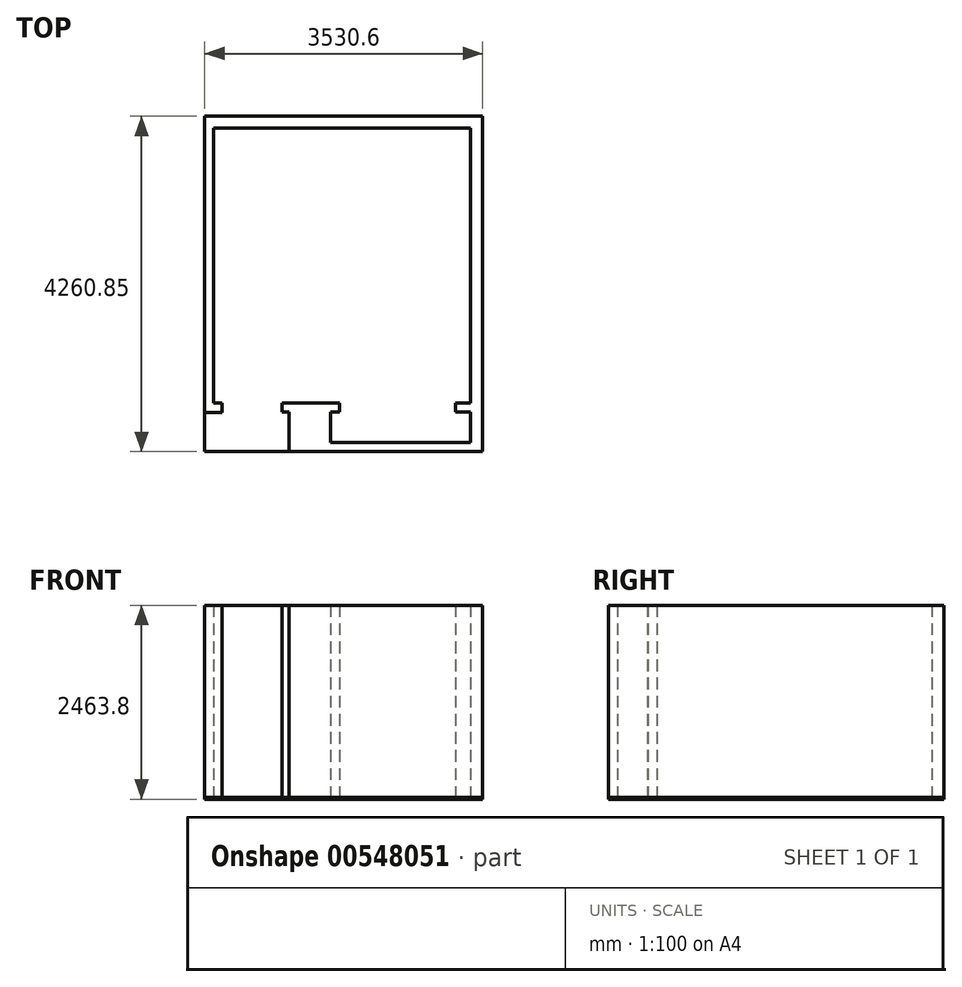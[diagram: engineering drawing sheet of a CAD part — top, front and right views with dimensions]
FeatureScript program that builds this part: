
annotation { "Feature Type Name" : "Feature", "Feature Type Description" : "" }
export const myFeature = defineFeature(function(context is Context, id is Id, definition is map)
    precondition{}
    {
        {
            var Q0;
            Q0=qCreatedBy(makeId("Top.planeOp"),FACE);
            var sketch = newSketch(context, id + "F0", { "sketchPlane" : qUnion([Q0])});
            skLineSegment(sketch, "E0.bottom", {"start": v(0, 0) * mm, "end": v(-3263.9, 0) * mm});
            skLineSegment(sketch, "E0.top", {"start": v(0, -3492.5) * mm, "end": v(-3263.9, -3492.5) * mm, "construction": true});
            skLineSegment(sketch, "E0.left", {"start": v(0, 0) * mm, "end": v(0, -3492.5) * mm});
            skLineSegment(sketch, "E0.right", {"start": v(-3263.9, 0) * mm, "end": v(-3263.9, -3492.5) * mm});
            skLineSegment(sketch, "E1.bottom", {"start": v(-3263.9, -3492.5) * mm, "end": v(-3158.55, -3492.5) * mm});
            skLineSegment(sketch, "E1.top", {"start": v(-3263.9, -3612.85) * mm, "end": v(-3158.55, -3612.85) * mm});
            skLineSegment(sketch, "E1.left", {"start": v(-3263.9, -3492.5) * mm, "end": v(-3263.9, -3612.85) * mm, "construction": true});
            skLineSegment(sketch, "E1.right", {"start": v(-3158.55, -3492.5) * mm, "end": v(-3158.55, -3612.85) * mm});
            skLineSegment(sketch, "E2.bottom", {"start": v(-2396.55, -3492.5) * mm, "end": v(-1663.7, -3492.5) * mm});
            skLineSegment(sketch, "E2.top", {"start": v(-2396.55, -3606.8) * mm, "end": v(-1663.7, -3606.8) * mm});
            skLineSegment(sketch, "E2.left", {"start": v(-2396.55, -3492.5) * mm, "end": v(-2396.55, -3606.8) * mm});
            skLineSegment(sketch, "E2.right", {"start": v(-1663.7, -3492.5) * mm, "end": v(-1663.7, -3606.8) * mm});
            skLineSegment(sketch, "E3.bottom", {"start": v(0, -3492.5) * mm, "end": v(-190.5, -3492.5) * mm});
            skLineSegment(sketch, "E3.top", {"start": v(0, -3606.8) * mm, "end": v(-190.5, -3606.8) * mm});
            skLineSegment(sketch, "E3.left", {"start": v(0, -3492.5) * mm, "end": v(0, -3606.8) * mm});
            skLineSegment(sketch, "E3.right", {"start": v(-190.5, -3492.5) * mm, "end": v(-190.5, -3606.8) * mm});
            skLineSegment(sketch, "E4.top", {"start": v(0, -3994.15) * mm, "end": v(-1780.52, -3994.15) * mm});
            skLineSegment(sketch, "E4.left", {"start": v(0, -3606.8) * mm, "end": v(0, -3994.15) * mm});
            skLineSegment(sketch, "E4.right", {"start": v(-1780.52, -3606.8) * mm, "end": v(-1780.52, -3994.15) * mm});
            skLineSegment(sketch, "E5", {"start": v(-3378.2, 152.4) * mm, "end": v(152.4, 152.4) * mm});
            skLineSegment(sketch, "E6", {"start": v(152.4, 152.4) * mm, "end": v(152.4, -4108.45) * mm});
            skLineSegment(sketch, "E7", {"start": v(152.4, -4108.45) * mm, "end": v(-2305.92, -4108.45) * mm});
            skLineSegment(sketch, "E8", {"start": v(-2305.92, -4108.45) * mm, "end": v(-2305.92, -3606.8) * mm});
            skLineSegment(sketch, "E9", {"start": v(-3378.2, 152.4) * mm, "end": v(-3378.2, -3612.85) * mm});
            skLineSegment(sketch, "E10", {"start": v(-3263.9, -3612.85) * mm, "end": v(-3378.2, -3612.85) * mm});
            skSolve(sketch);
        }
        {
            var Q0;
            Q0 = qSketchRegion(id + "F0", true);
            extrude(context, id + "F1", {"entities" : qUnion([Q0]), "depth" : 2438.4 * mm, "offsetDistance" : 25.4 * mm});
        }
        {
            var Q0;
            Q0=makeQuery(id+"F1.opExtrude","CAP_FACE",FACE,{"disambiguationData":[OSD([sQuery(id+"F0.wireOp",EDGE,"E0.bottom"),sQuery(id+"F0.wireOp",EDGE,"E0.left"),sQuery(id+"F0.wireOp",EDGE,"E0.right"),sQuery(id+"F0.wireOp",EDGE,"E1.bottom"),sQuery(id+"F0.wireOp",EDGE,"E1.top"),sQuery(id+"F0.wireOp",EDGE,"E1.right"),sQuery(id+"F0.wireOp",EDGE,"E2.bottom"),sQuery(id+"F0.wireOp",EDGE,"E2.top"),sQuery(id+"F0.wireOp",EDGE,"E2.left"),sQuery(id+"F0.wireOp",EDGE,"E2.right"),sQuery(id+"F0.wireOp",EDGE,"E3.bottom"),sQuery(id+"F0.wireOp",EDGE,"E3.top"),sQuery(id+"F0.wireOp",EDGE,"E3.right"),sQuery(id+"F0.wireOp",EDGE,"E4.top"),sQuery(id+"F0.wireOp",EDGE,"E4.left"),sQuery(id+"F0.wireOp",EDGE,"E4.right"),sQuery(id+"F0.wireOp",EDGE,"E5"),sQuery(id+"F0.wireOp",EDGE,"E6"),sQuery(id+"F0.wireOp",EDGE,"E7"),sQuery(id+"F0.wireOp",EDGE,"E8"),sQuery(id+"F0.wireOp",EDGE,"E9"),sQuery(id+"F0.wireOp",EDGE,"E10")])],"isStart":true});
            var sketch = newSketch(context, id + "F2", { "sketchPlane" : qUnion([Q0])});
            skLineSegment(sketch, "E11.bottom", {"start": v(152.4, 4108.45) * mm, "end": v(-3378.2, 4108.45) * mm});
            skLineSegment(sketch, "E11.top", {"start": v(152.4, -152.4) * mm, "end": v(-3378.2, -152.4) * mm});
            skLineSegment(sketch, "E11.left", {"start": v(152.4, 4108.45) * mm, "end": v(152.4, -152.4) * mm});
            skLineSegment(sketch, "E11.right", {"start": v(-3378.2, 4108.45) * mm, "end": v(-3378.2, -152.4) * mm});
            skSolve(sketch);
        }
        {
            var Q0;
            Q0 = qSketchRegion(id + "F2", true);
            extrude(context, id + "F3", {"entities" : qUnion([Q0]), "depth" : 25.4 * mm, "offsetDistance" : 25.4 * mm});
        }
    });
